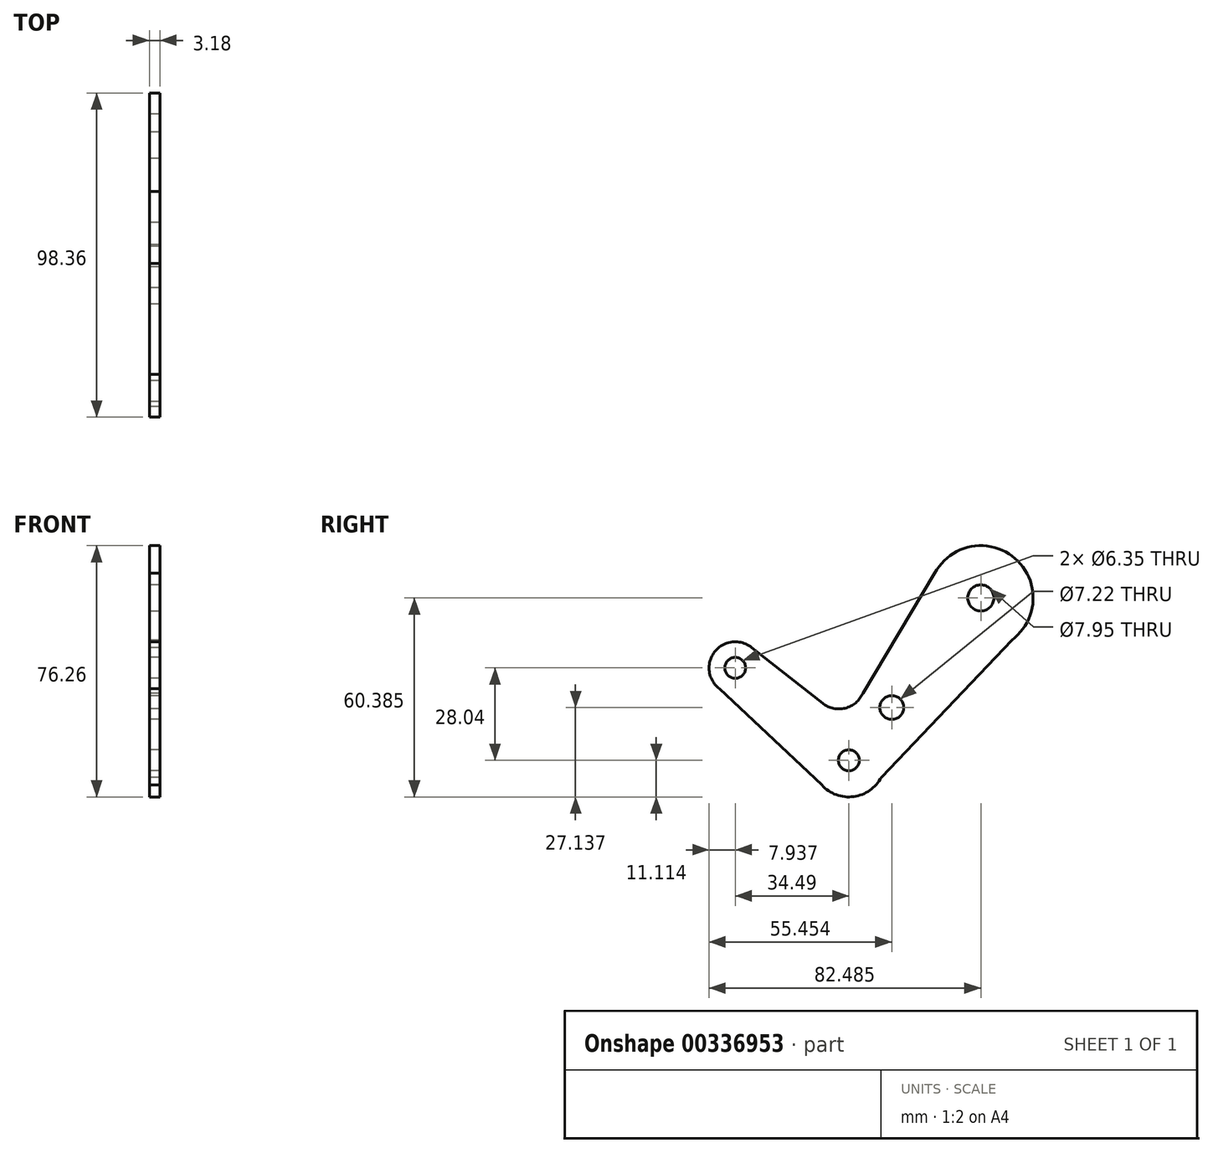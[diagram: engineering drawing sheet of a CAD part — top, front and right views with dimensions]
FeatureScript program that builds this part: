
annotation { "Feature Type Name" : "Feature", "Feature Type Description" : "" }
export const myFeature = defineFeature(function(context is Context, id is Id, definition is map)
    precondition{}
    {
        {
            var Q0;
            Q0=qCreatedBy(makeId("Right.planeOp"),FACE);
            var sketch = newSketch(context, id + "F0", { "sketchPlane" : qUnion([Q0])});
            skCircle(sketch, "E0", {"center": v(-50.4, 49.27) * mm, "radius": 7.94 * mm});
            skCircle(sketch, "E1", {"center": v(-50.4, 49.27) * mm, "radius": 3.18 * mm});
            skCircle(sketch, "E2", {"center": v(-27.59, 11.13) * mm, "radius": 11.11 * mm});
            skCircle(sketch, "E3", {"center": v(-27.59, 11.13) * mm, "radius": 3.18 * mm});
            skCircle(sketch, "E4", {"center": v(-9.87, 21.73) * mm, "radius": 3.61 * mm});
            skLineSegment(sketch, "E5", {"start": v(-50.4, 49.27) * mm, "end": v(-27.59, 11.13) * mm});
            skLineSegment(sketch, "E6", {"start": v(-9.87, 21.73) * mm, "end": v(-27.59, 11.13) * mm});
            skCircle(sketch, "E7", {"center": v(26.9, 43.72) * mm, "radius": 15.88 * mm});
            skLineSegment(sketch, "E8", {"start": v(-9.87, 21.73) * mm, "end": v(26.9, 43.72) * mm});
            skCircle(sketch, "E9", {"center": v(26.9, 43.72) * mm, "radius": 3.98 * mm});
            skCircle(sketch, "E10", {"center": v(26.9, 43.72) * mm, "radius": 3.18 * mm});
            skPoint(sketch, "E11", {"position": v(-43.6, 53.35) * mm});
            skPoint(sketch, "E12", {"position": v(-57.06, 44.94) * mm});
            skPoint(sketch, "E13", {"position": v(-37.13, 5.42) * mm});
            skPoint(sketch, "E14", {"position": v(-20.09, 2.93) * mm});
            skPoint(sketch, "E15", {"position": v(17.48, 56.5) * mm});
            skPoint(sketch, "E16", {"position": v(36.33, 30.95) * mm});
            skLineSegment(sketch, "E17", {"start": v(-57.06, 44.94) * mm, "end": v(-37.13, 5.42) * mm});
            skLineSegment(sketch, "E18", {"start": v(-20.09, 2.93) * mm, "end": v(36.33, 30.95) * mm});
            skPoint(sketch, "E19", {"position": v(-29.14, 30.09) * mm});
            skPoint(sketch, "E20", {"position": v(-16.65, 28.78) * mm});
            skLineSegment(sketch, "E21", {"start": v(-43.6, 53.35) * mm, "end": v(-29.14, 30.09) * mm});
            skLineSegment(sketch, "E22", {"start": v(-16.65, 28.78) * mm, "end": v(17.48, 56.5) * mm});
            skArc(sketch, "E23", {"start": v(-29.14, 30.09) * mm, "mid": v(-23.22, 26.38) * mm, "end": v(-16.65, 28.78) * mm});
            skSolve(sketch);
        }
        {
            var Q0;
            Q0 = qSketchRegion(id + "F0", true);
            var Q1;
            {var subQ0=sQuery(id+"F0.wireOp",EDGE,"E5");var subQ1=sQuery(id+"F0.wireOp",EDGE,"E2");var subQ2=makeQuery(id+"F0.imprint","INTERSECT",VERTEX,{"derivedFrom":[subQ1,subQ0]});Q1=makeQuery(id+"F0.imprint","IMPRINT",FACE,{"disambiguationData":[TD([[makeQuery(id+"F0.imprint","IMPRINT",EDGE,{"disambiguationData":[TD([[subQ2,1.0]])],"derivedFrom":subQ1}),1.0]])]});}
            extrude(context, id + "F1", {"entities" : qUnion([Q0, Q1]), "depth" : 3.17 * mm});
        }
        {
            var Q0;
            Q0=makeQuery(id+"F1.opExtrude","SWEPT_BODY",BODY,{"disambiguationData":[OSD([sQuery(id+"F0.wireOp",EDGE,"E0"),sQuery(id+"F0.wireOp",EDGE,"E1"),sQuery(id+"F0.wireOp",EDGE,"E2"),sQuery(id+"F0.wireOp",EDGE,"E3"),sQuery(id+"F0.wireOp",EDGE,"E4"),sQuery(id+"F0.wireOp",EDGE,"E7"),sQuery(id+"F0.wireOp",EDGE,"E9"),sQuery(id+"F0.wireOp",EDGE,"E17"),sQuery(id+"F0.wireOp",EDGE,"E18"),sQuery(id+"F0.wireOp",EDGE,"E21"),sQuery(id+"F0.wireOp",EDGE,"E22"),sQuery(id+"F0.wireOp",EDGE,"E23")])]});
            var Q1;
            Q1=sQuery(id+"F0.wireOp",EDGE,"E7");
            transform(context, id + "F2", {"entities" : qUnion([Q0]), "transformType" : TransformType.ROTATION, "transformAxis" : qUnion([Q1]), "angle" : 20 * degree, "makeCopy" : false});
        }
    });
